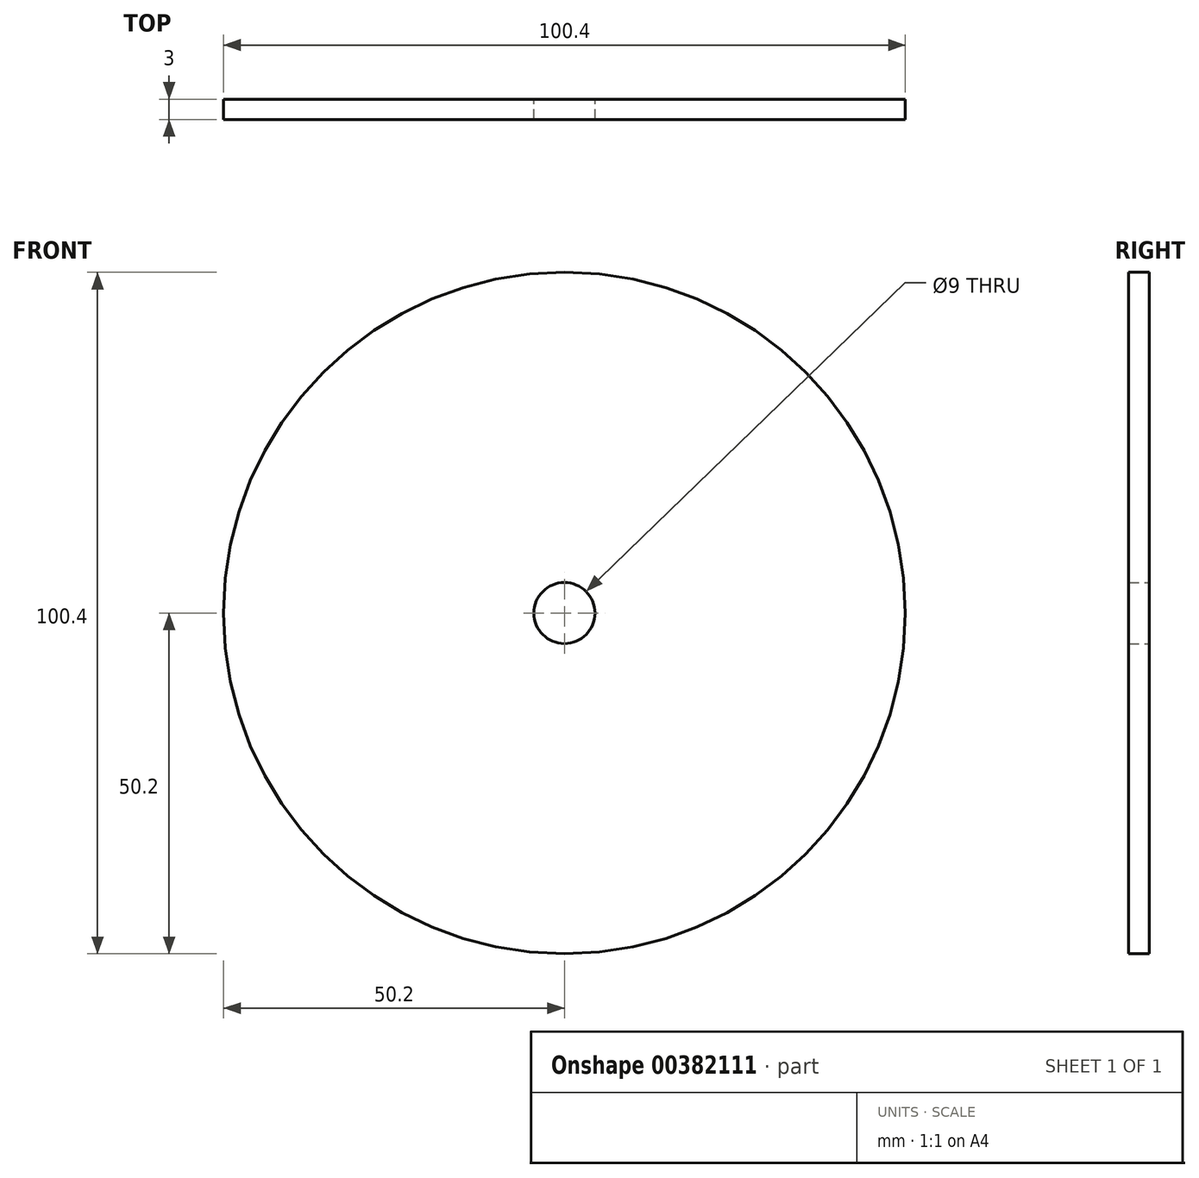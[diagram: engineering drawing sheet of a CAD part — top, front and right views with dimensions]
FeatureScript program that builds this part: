
annotation { "Feature Type Name" : "Feature", "Feature Type Description" : "" }
export const myFeature = defineFeature(function(context is Context, id is Id, definition is map)
    precondition{}
    {
        {
            var Q0;
            Q0=qCreatedBy(makeId("Front.planeOp"),FACE);
            var sketch = newSketch(context, id + "F0", { "sketchPlane" : qUnion([Q0])});
            skCircle(sketch, "E0", {"center": v(0, 0) * mm, "radius": 50.2 * mm});
            skCircle(sketch, "E1", {"center": v(0, 0) * mm, "radius": 4.5 * mm});
            skSolve(sketch);
        }
        {
            var Q0;
            Q0 = qSketchRegion(id + "F0", true);
            extrude(context, id + "F1", {"entities" : qUnion([Q0]), "depth" : 3 * mm});
        }
    });
